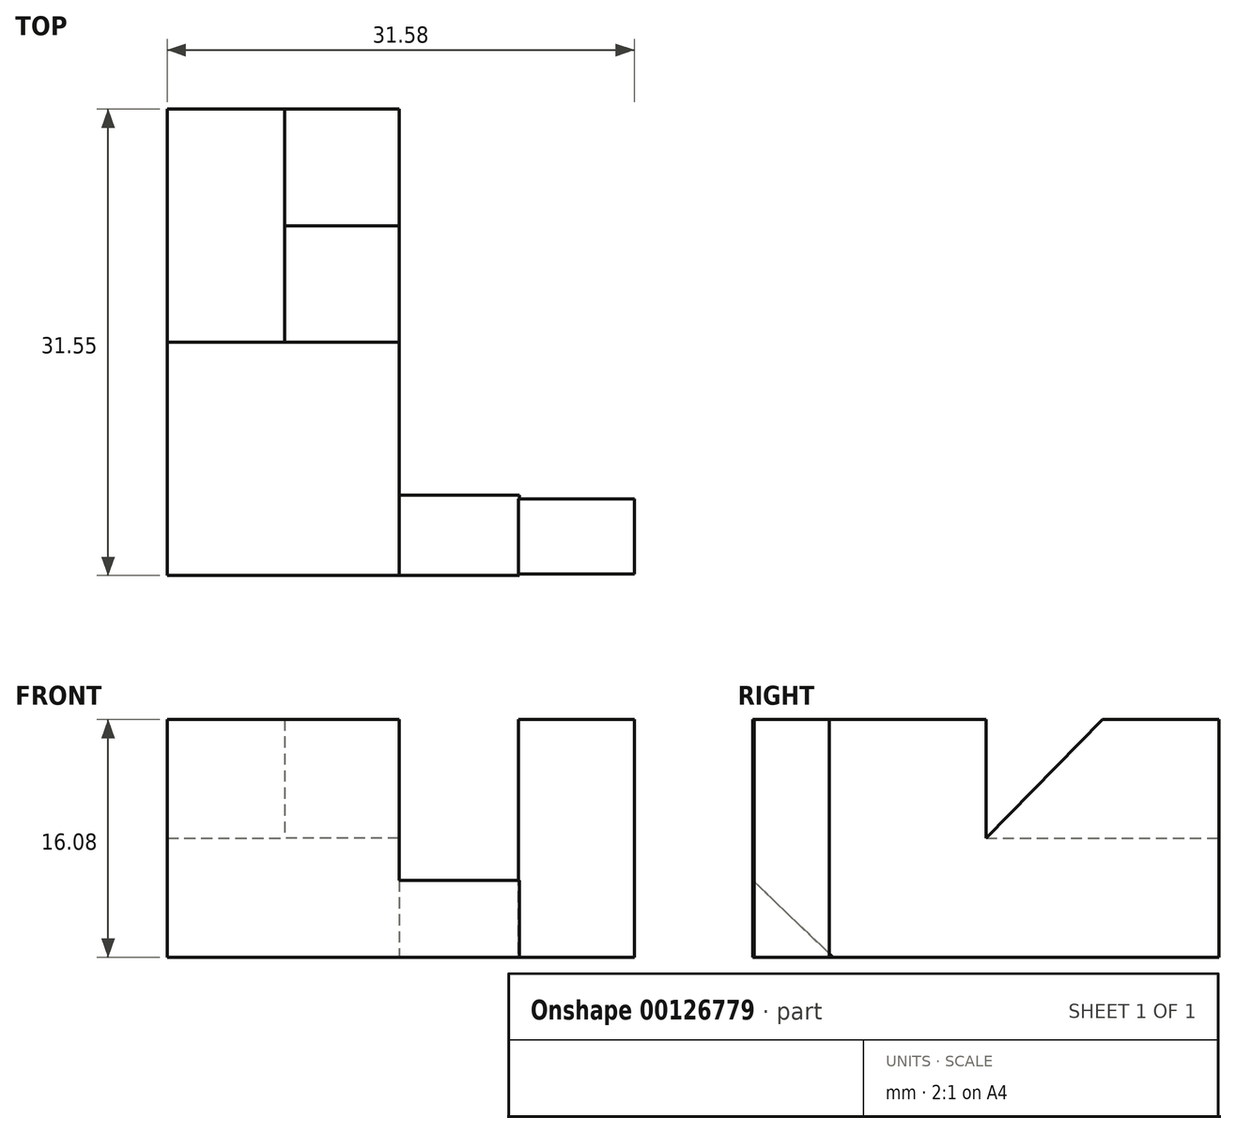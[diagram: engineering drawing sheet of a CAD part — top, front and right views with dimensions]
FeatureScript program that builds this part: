
annotation { "Feature Type Name" : "Feature", "Feature Type Description" : "" }
export const myFeature = defineFeature(function(context is Context, id is Id, definition is map)
    precondition{}
    {
        {
            var Q0;
            Q0=qCreatedBy(makeId("Top.planeOp"),FACE);
            var sketch = newSketch(context, id + "F0", { "sketchPlane" : qUnion([Q0])});
            skLineSegment(sketch, "E0.bottom", {"start": v(-5.82, 26.11) * mm, "end": v(9.85, 26.11) * mm});
            skLineSegment(sketch, "E0.top", {"start": v(-5.82, -5.44) * mm, "end": v(9.85, -5.44) * mm});
            skLineSegment(sketch, "E0.left", {"start": v(-5.82, 26.11) * mm, "end": v(-5.82, -5.44) * mm});
            skLineSegment(sketch, "E0.right", {"start": v(9.85, 26.11) * mm, "end": v(9.85, -5.44) * mm});
            skLineSegment(sketch, "E1", {"start": v(-5.82, 10.34) * mm, "end": v(9.85, 10.34) * mm});
            skLineSegment(sketch, "E2.left", {"start": v(9.85, 0) * mm, "end": v(9.85, -5.46) * mm});
            skSolve(sketch);
        }
        {
            var Q0;
            {var subQ0=sQuery(id+"F0.wireOp",EDGE,"E0.top");Q0=makeQuery(id+"F0.imprint","IMPRINT",FACE,{"disambiguationData":[TD([[makeQuery(id+"F0.imprint","IMPRINT",EDGE,{"derivedFrom":subQ0}),1.0]])]});}
            extrude(context, id + "F1", {"entities" : qUnion([Q0]), "depth" : 16.08 * mm});
        }
        {
            var Q0;
            {var subQ0=sQuery(id+"F0.wireOp",EDGE,"E0.bottom");Q0=makeQuery(id+"F0.imprint","IMPRINT",FACE,{"disambiguationData":[TD([[makeQuery(id+"F0.imprint","IMPRINT",EDGE,{"derivedFrom":subQ0}),-1.0]])]});}
            extrude(context, id + "F2", {"entities" : qUnion([Q0]), "operationType" : NewBodyOperationType.ADD, "depth" : 8.05 * mm});
        }
        {
            var Q0;
            {var subQ0=sQuery(id+"F0.wireOp",EDGE,"E0.right");Q0=makeQuery(id+"F2.boolean.opBoolean","MERGE",FACE,{"derivedFrom":[makeQuery(id+"F1.opExtrude","SWEPT_FACE",FACE,{"disambiguationData":[OSD([subQ0,sQuery(id+"F0.wireOp",EDGE,"E2.left")])]}),makeQuery(id+"F2.opExtrude","SWEPT_FACE",FACE,{"disambiguationData":[OSD([subQ0])]})]});}
            var sketch = newSketch(context, id + "F3", { "sketchPlane" : qUnion([Q0])});
            skLineSegment(sketch, "E3", {"start": v(-5.44, 5.2) * mm, "end": v(0, 0) * mm});
            skSolve(sketch);
        }
        {
            var Q0;
            {var subQ0=sQuery(id+"F3.wireOp",EDGE,"E3");Q0=makeQuery(id+"F3.imprint","IMPRINT",FACE,{"disambiguationData":[TD([[makeQuery(id+"F3.imprint","IMPRINT",EDGE,{"derivedFrom":subQ0}),-1.0]])]});}
            extrude(context, id + "F4", {"entities" : qUnion([Q0]), "operationType" : NewBodyOperationType.ADD, "depth" : 8.15 * mm});
        }
        {
            var Q0;
            Q0=qCreatedBy(makeId("Top.planeOp"),FACE);
            var sketch = newSketch(context, id + "F5", { "sketchPlane" : qUnion([Q0])});
            skLineSegment(sketch, "E4.bottom", {"start": v(17.91, -5.34) * mm, "end": v(25.76, -5.34) * mm});
            skLineSegment(sketch, "E4.top", {"start": v(17.91, -0.26) * mm, "end": v(25.76, -0.26) * mm});
            skLineSegment(sketch, "E4.left", {"start": v(17.91, -5.34) * mm, "end": v(17.91, -0.26) * mm});
            skLineSegment(sketch, "E4.right", {"start": v(25.76, -5.34) * mm, "end": v(25.76, -0.26) * mm});
            skSolve(sketch);
        }
        {
            var Q0;
            Q0 = qSketchRegion(id + "F5", true);
            var Q1;
            Q1=makeQuery(id+"F1.opExtrude","CAP_FACE",FACE,{"disambiguationData":[OSD([sQuery(id+"F0.wireOp",EDGE,"E0.top"),sQuery(id+"F0.wireOp",EDGE,"E0.left"),sQuery(id+"F0.wireOp",EDGE,"E0.right"),sQuery(id+"F0.wireOp",EDGE,"E1"),sQuery(id+"F0.wireOp",EDGE,"E2.left")])],"isStart":false});
            extrude(context, id + "F6", {"entities" : qUnion([Q0]), "operationType" : NewBodyOperationType.ADD, "endBound" : BoundingType.UP_TO_SURFACE, "endBoundEntityFace" : qUnion([Q1]), "depth" : 15.65 * mm});
        }
        {
            var Q0;
            Q0=makeQuery(id+"F2.opExtrude","CAP_FACE",FACE,{"disambiguationData":[OSD([sQuery(id+"F0.wireOp",EDGE,"E0.bottom"),sQuery(id+"F0.wireOp",EDGE,"E0.left"),sQuery(id+"F0.wireOp",EDGE,"E0.right"),sQuery(id+"F0.wireOp",EDGE,"E1")])],"isStart":false});
            var sketch = newSketch(context, id + "F7", { "sketchPlane" : qUnion([Q0])});
            skLineSegment(sketch, "E5.bottom", {"start": v(9.85, 10.34) * mm, "end": v(2.1, 10.34) * mm});
            skLineSegment(sketch, "E5.top", {"start": v(9.85, 26.11) * mm, "end": v(2.1, 26.11) * mm});
            skLineSegment(sketch, "E5.left", {"start": v(9.85, 10.34) * mm, "end": v(9.85, 26.11) * mm});
            skLineSegment(sketch, "E5.right", {"start": v(2.1, 10.34) * mm, "end": v(2.1, 26.11) * mm});
            skLineSegment(sketch, "E6", {"start": v(9.85, 18.22) * mm, "end": v(2.1, 18.22) * mm});
            skSolve(sketch);
        }
        {
            var Q0;
            {var subQ0=sQuery(id+"F7.wireOp",EDGE,"E5.top");Q0=makeQuery(id+"F7.imprint","IMPRINT",FACE,{"disambiguationData":[TD([[makeQuery(id+"F7.imprint","IMPRINT",EDGE,{"derivedFrom":subQ0}),-1.0]])]});}
            var Q1;
            Q1=makeQuery(id+"F1.opExtrude","CAP_FACE",FACE,{"disambiguationData":[OSD([sQuery(id+"F0.wireOp",EDGE,"E0.top"),sQuery(id+"F0.wireOp",EDGE,"E0.left"),sQuery(id+"F0.wireOp",EDGE,"E0.right"),sQuery(id+"F0.wireOp",EDGE,"E1"),sQuery(id+"F0.wireOp",EDGE,"E2.left")])],"isStart":false});
            extrude(context, id + "F8", {"entities" : qUnion([Q0]), "operationType" : NewBodyOperationType.ADD, "endBound" : BoundingType.UP_TO_SURFACE, "endBoundEntityFace" : qUnion([Q1]), "depth" : 3.1 * mm});
        }
        {
            var Q0;
            Q0=makeQuery(id+"F8.opExtrude","SWEPT_FACE",FACE,{"disambiguationData":[OSD([sQuery(id+"F7.wireOp",EDGE,"E5.right")])]});
            var sketch = newSketch(context, id + "F9", { "sketchPlane" : qUnion([Q0])});
            skPoint(sketch, "E7.0", {"position": v(-18.22, 16.08) * mm});
            skLineSegment(sketch, "E8.0", {"start": v(-10.34, 16.08) * mm, "end": v(-10.34, 8.05) * mm});
            skLineSegment(sketch, "E8.1", {"start": v(-26.11, 8.05) * mm, "end": v(-10.34, 8.05) * mm});
            skLineSegment(sketch, "E9", {"start": v(-18.22, 16.08) * mm, "end": v(-10.34, 8.05) * mm});
            skSolve(sketch);
        }
        {
            var Q0;
            {var subQ2=sQuery(id+"F9.wireOp",EDGE,"E9");Q0=makeQuery(id+"F9.imprint","IMPRINT",FACE,{"disambiguationData":[TD([[makeQuery(id+"F9.imprint","IMPRINT",EDGE,{"derivedFrom":subQ2}),-1.0]])]});}
            var Q1;
            {var subQ0=sQuery(id+"F0.wireOp",EDGE,"E0.right");Q1=makeQuery(id+"F8.boolean.opBoolean","MERGE",FACE,{"derivedFrom":[makeQuery(id+"F2.boolean.opBoolean","MERGE",FACE,{"derivedFrom":[makeQuery(id+"F1.opExtrude","SWEPT_FACE",FACE,{"disambiguationData":[OSD([subQ0,sQuery(id+"F0.wireOp",EDGE,"E2.left")])]}),makeQuery(id+"F2.opExtrude","SWEPT_FACE",FACE,{"disambiguationData":[OSD([subQ0])]})]}),makeQuery(id+"F8.opExtrude","SWEPT_FACE",FACE,{"disambiguationData":[OSD([sQuery(id+"F7.wireOp",EDGE,"E5.left")])]})]});}
            extrude(context, id + "F10", {"entities" : qUnion([Q0]), "operationType" : NewBodyOperationType.ADD, "endBound" : BoundingType.UP_TO_SURFACE, "oppositeDirection" : true, "endBoundEntityFace" : qUnion([Q1]), "depth" : 25.4 * mm});
        }
    });
